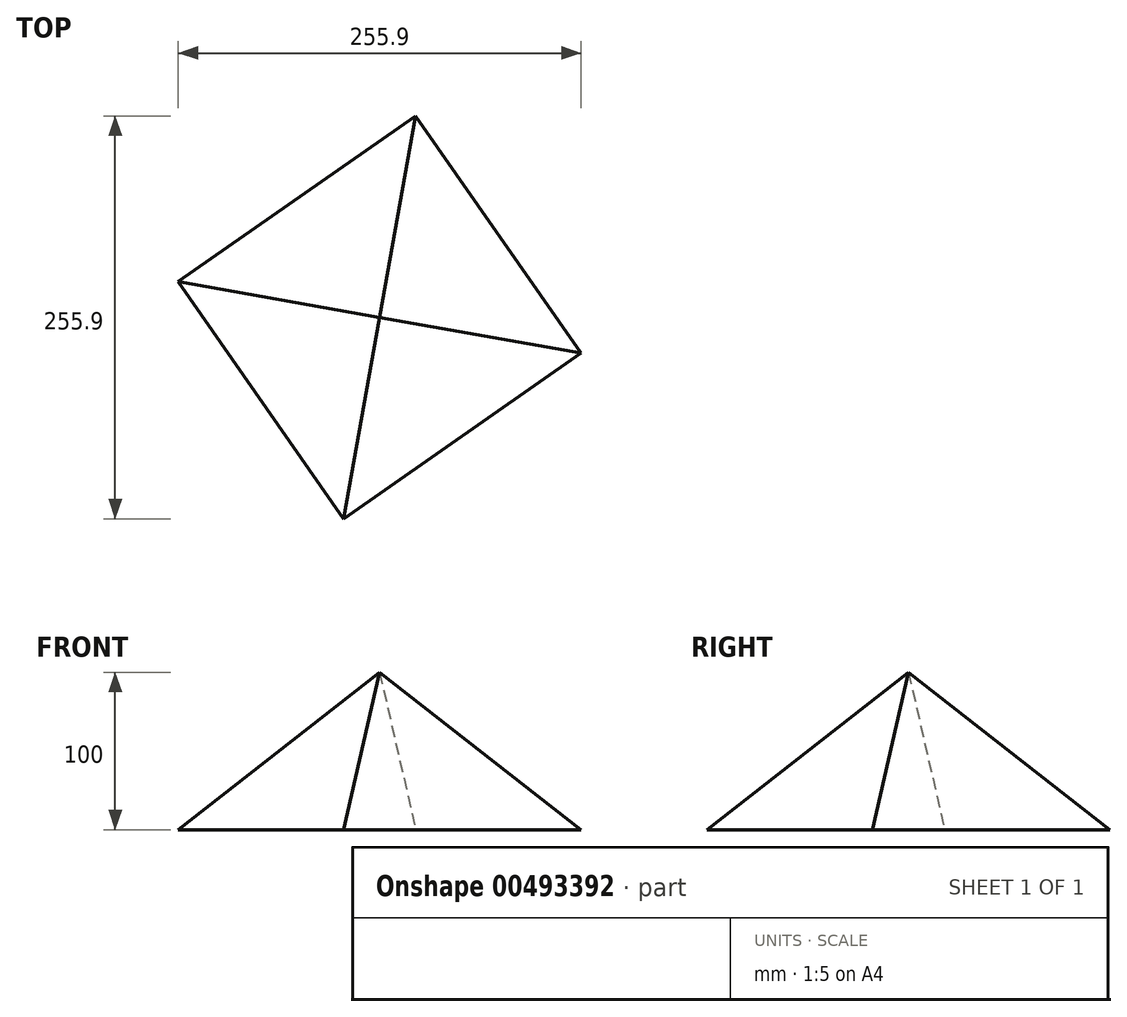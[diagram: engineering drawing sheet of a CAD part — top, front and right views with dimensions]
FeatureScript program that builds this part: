
annotation { "Feature Type Name" : "Feature", "Feature Type Description" : "" }
export const myFeature = defineFeature(function(context is Context, id is Id, definition is map)
    precondition{}
    {
        {
            var Q0;
            Q0=qCreatedBy(makeId("Top.planeOp"),FACE);
            var sketch = newSketch(context, id + "F0", { "sketchPlane" : qUnion([Q0])});
            skCircle(sketch, "E0.cCircle", {"center": v(0, 0) * mm, "radius": 129.97 * mm, "construction": true});
            skLineSegment(sketch, "E0.0", {"start": v(-127.95, 22.8) * mm, "end": v(22.8, 127.95) * mm});
            skLineSegment(sketch, "E0.1", {"start": v(22.8, 127.95) * mm, "end": v(127.95, -22.8) * mm});
            skLineSegment(sketch, "E0.2", {"start": v(127.95, -22.8) * mm, "end": v(-22.8, -127.95) * mm});
            skLineSegment(sketch, "E0.3", {"start": v(-22.8, -127.95) * mm, "end": v(-127.95, 22.8) * mm});
            skSolve(sketch);
        }
        {
            var Q0;
            Q0=qCreatedBy(makeId("Top.planeOp"),FACE);
            cPlane(context, id + "F1", {"entities" : qUnion([Q0]), "cplaneType" : CPlaneType.OFFSET, "offset" : 100 * mm, "width" : 150 * mm, "height" : 150 * mm});
        }
        {
            var Q0;
            Q0=qCreatedBy(id+"F1.planeOp",FACE);
            var sketch = newSketch(context, id + "F2", { "sketchPlane" : qUnion([Q0])});
            skPoint(sketch, "E1", {"position": v(0, 0) * mm});
            skSolve(sketch);
        }
        {
            var Q0;
            Q0=sQuery(id+"F2.wireOp",VERTEX,"E1");
            var Q1;
            Q1=makeQuery(id+"F0.imprint","IMPRINT",FACE,{"disambiguationData":[TD([[makeQuery(id+"F0.imprint","IMPRINT",EDGE,{"derivedFrom":sQuery(id+"F0.wireOp",EDGE,"E0.0")}),-1.0]])]});
            loft(context, id + "F3", {"sheetProfilesArray" : [{ "sheetProfileEntities" : qUnion([Q0]) }, { "sheetProfileEntities" : qUnion([Q1]) }]});
        }
    });
